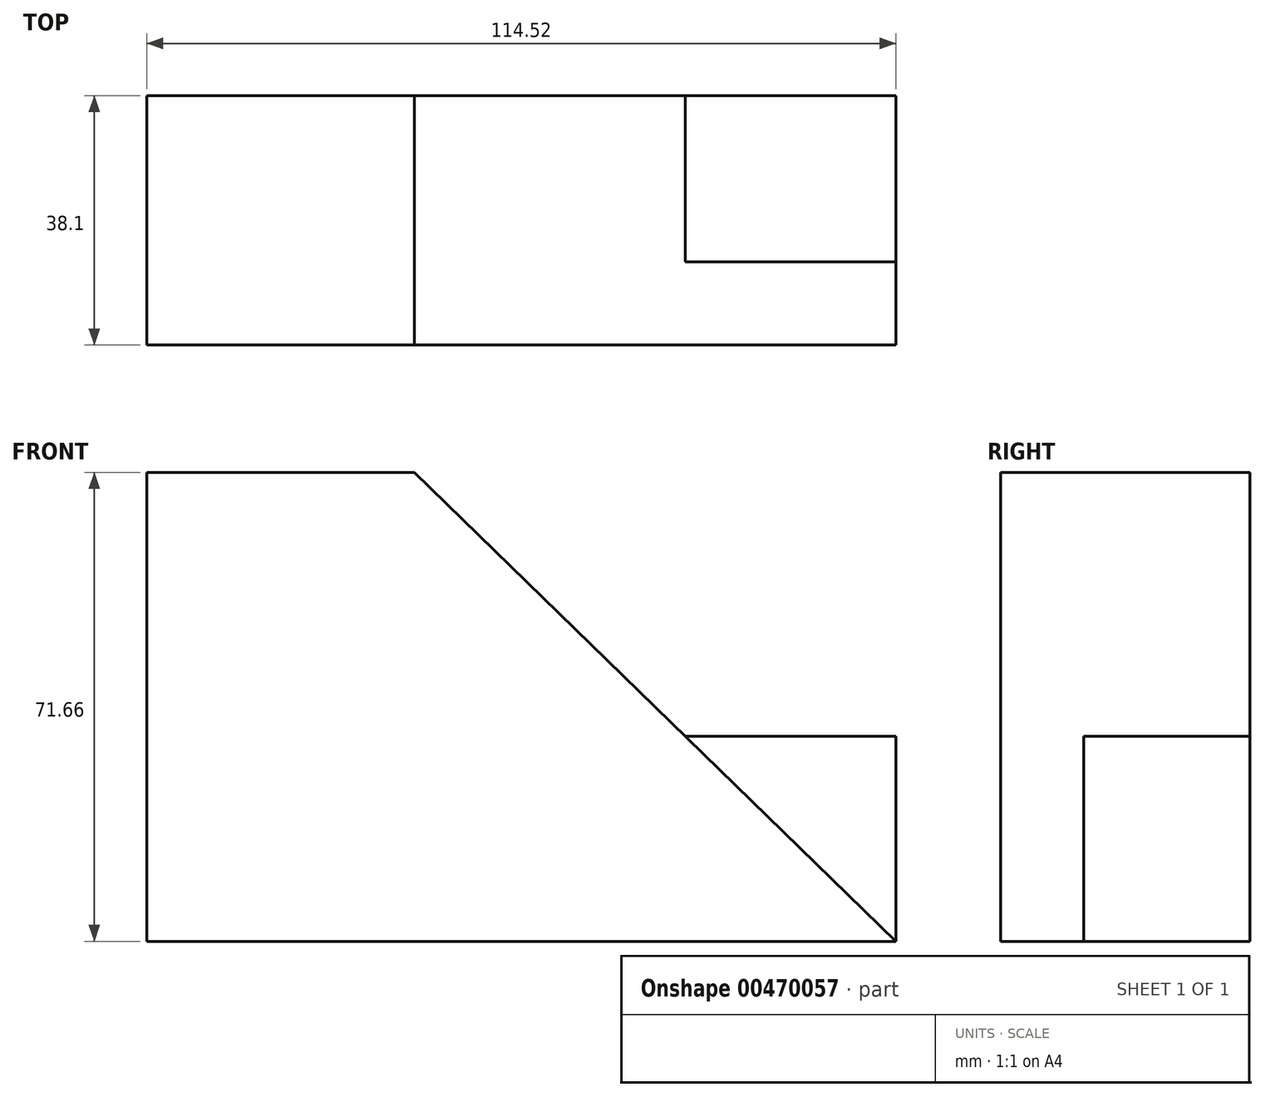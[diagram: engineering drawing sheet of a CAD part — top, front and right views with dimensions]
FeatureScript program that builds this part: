
annotation { "Feature Type Name" : "Feature", "Feature Type Description" : "" }
export const myFeature = defineFeature(function(context is Context, id is Id, definition is map)
    precondition{}
    {
        {
            var Q0;
            Q0=qCreatedBy(makeId("Front.planeOp"),FACE);
            var sketch = newSketch(context, id + "F0", { "sketchPlane" : qUnion([Q0])});
            skLineSegment(sketch, "E0.bottom", {"start": v(-16.3, 35.83) * mm, "end": v(-57.26, 35.83) * mm});
            skLineSegment(sketch, "E0.top", {"start": v(57.26, -35.83) * mm, "end": v(-57.26, -35.83) * mm});
            skLineSegment(sketch, "E0.left", {"start": v(57.26, -4.5) * mm, "end": v(57.26, -35.83) * mm});
            skLineSegment(sketch, "E0.right", {"start": v(-57.26, 35.83) * mm, "end": v(-57.26, -35.83) * mm});
            skPoint(sketch, "E0.middle", {"position": v(0, 0) * mm});
            skLineSegment(sketch, "E1", {"start": v(-16.3, 35.83) * mm, "end": v(57.26, -35.83) * mm});
            skLineSegment(sketch, "E2", {"start": v(25.1, -4.5) * mm, "end": v(57.26, -4.5) * mm});
            skPoint(sketch, "E3.orphan", {"position": v(57.26, 35.83) * mm});
            skSolve(sketch);
        }
        {
            var Q0;
            {var subQ1=sQuery(id+"F0.wireOp",EDGE,"E0.bottom");Q0=makeQuery(id+"F0.imprint","IMPRINT",FACE,{"disambiguationData":[TD([[makeQuery(id+"F0.imprint","IMPRINT",EDGE,{"derivedFrom":subQ1}),1.0]])]});}
            extrude(context, id + "F1", {"entities" : qUnion([Q0]), "depth" : 38.1 * mm});
        }
        {
            var Q0;
            {var subQ0=sQuery(id+"F0.wireOp",EDGE,"E0.left");Q0=makeQuery(id+"F0.imprint","IMPRINT",FACE,{"disambiguationData":[TD([[makeQuery(id+"F0.imprint","IMPRINT",EDGE,{"derivedFrom":subQ0}),-1.0]])]});}
            extrude(context, id + "F2", {"entities" : qUnion([Q0]), "operationType" : NewBodyOperationType.ADD, "depth" : 25.4 * mm});
        }
    });
